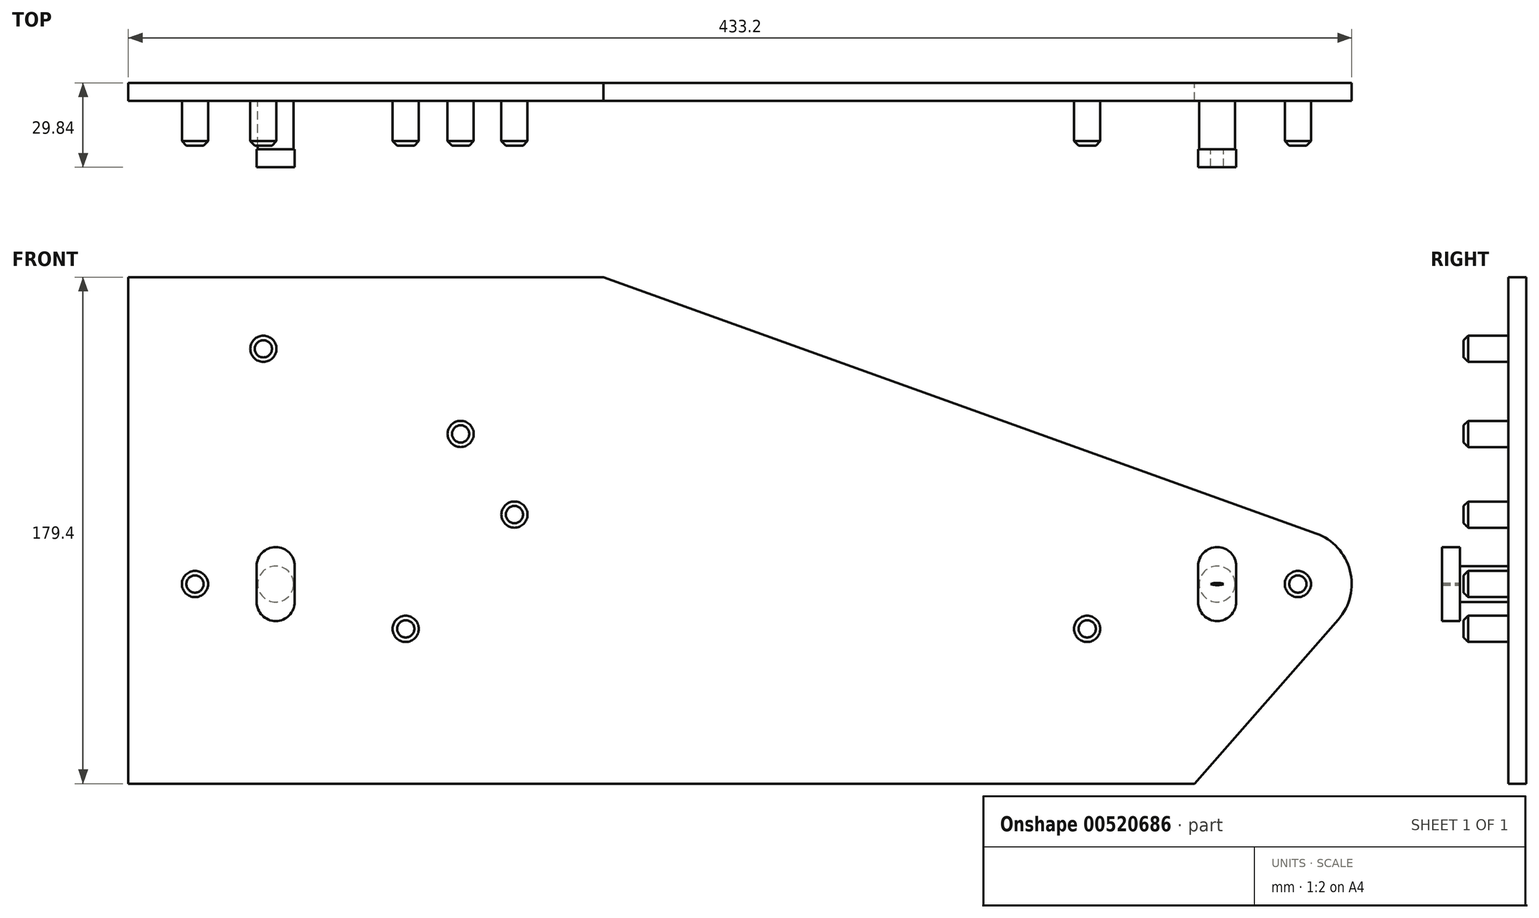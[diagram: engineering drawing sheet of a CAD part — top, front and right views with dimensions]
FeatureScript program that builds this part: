
annotation { "Feature Type Name" : "Feature", "Feature Type Description" : "" }
export const myFeature = defineFeature(function(context is Context, id is Id, definition is map)
    precondition{}
    {
        {
            var Q0;
            Q0=qCreatedBy(makeId("Front.planeOp"),FACE);
            var sketch = newSketch(context, id + "F0", { "sketchPlane" : qUnion([Q0])});
            skLineSegment(sketch, "E0", {"start": v(0, 0) * mm, "end": v(0, 179.4) * mm});
            skLineSegment(sketch, "E1", {"start": v(0, 0) * mm, "end": v(377.52, 0) * mm});
            skLineSegment(sketch, "E2", {"start": v(0, 179.4) * mm, "end": v(168.28, 179.4) * mm});
            skLineSegment(sketch, "E3", {"start": v(168.27, 179.4) * mm, "end": v(420.6, 88.65) * mm});
            skLineSegment(sketch, "E4", {"start": v(377.52, 0) * mm, "end": v(428.48, 58.18) * mm});
            skPoint(sketch, "E5.visualSharp", {"position": v(446.89, 79.2) * mm});
            skArc(sketch, "E5.filletArc", {"start": v(428.48, 58.18) * mm, "mid": v(432.59, 75.5) * mm, "end": v(420.6, 88.65) * mm});
            skSolve(sketch);
        }
        {
            var Q0;
            Q0 = qSketchRegion(id + "F0", true);
            extrude(context, id + "F1", {"entities" : qUnion([Q0]), "endBound" : BoundingType.SYMMETRIC, "depth" : 6.35 * mm, "offsetDistance" : 25.4 * mm});
        }
        {
            var Q0;
            Q0=makeQuery(id+"F1.opExtrude","CAP_FACE",FACE,{"disambiguationData":[OSD([sQuery(id+"F0.wireOp",EDGE,"E0"),sQuery(id+"F0.wireOp",EDGE,"E1"),sQuery(id+"F0.wireOp",EDGE,"E2"),sQuery(id+"F0.wireOp",EDGE,"E3"),sQuery(id+"F0.wireOp",EDGE,"E4"),sQuery(id+"F0.wireOp",EDGE,"E5.filletArc")])],"isStart":false});
            var sketch = newSketch(context, id + "F2", { "sketchPlane" : qUnion([Q0])});
            skCircle(sketch, "E6", {"center": v(23.62, 70.71) * mm, "radius": 4.64 * mm});
            skCircle(sketch, "E7", {"center": v(98.22, 54.84) * mm, "radius": 4.64 * mm});
            skCircle(sketch, "E8", {"center": v(339.52, 54.84) * mm, "radius": 4.64 * mm});
            skCircle(sketch, "E9", {"center": v(136.73, 95.33) * mm, "radius": 4.64 * mm});
            skCircle(sketch, "E10", {"center": v(47.83, 154.05) * mm, "radius": 4.64 * mm});
            skCircle(sketch, "E11", {"center": v(117.68, 123.9) * mm, "radius": 4.64 * mm});
            skCircle(sketch, "E12", {"center": v(414.15, 70.71) * mm, "radius": 4.64 * mm});
            skSolve(sketch);
        }
        {
            var Q0;
            Q0 = qSketchRegion(id + "F2", true);
            extrude(context, id + "F3", {"entities" : qUnion([Q0]), "operationType" : NewBodyOperationType.ADD, "depth" : 15.88 * mm, "offsetDistance" : 25.4 * mm});
        }
        {
            var Q0;
            Q0=makeQuery(id+"F3.opExtrude","CAP_EDGE",EDGE,{"disambiguationData":[OSD([sQuery(id+"F2.wireOp",EDGE,"E6")])],"isStart":false});
            var Q1;
            Q1=makeQuery(id+"F3.opExtrude","CAP_EDGE",EDGE,{"disambiguationData":[OSD([sQuery(id+"F2.wireOp",EDGE,"E10")])],"isStart":false});
            var Q2;
            Q2=makeQuery(id+"F3.opExtrude","CAP_EDGE",EDGE,{"disambiguationData":[OSD([sQuery(id+"F2.wireOp",EDGE,"E7")])],"isStart":false});
            var Q3;
            Q3=makeQuery(id+"F3.opExtrude","CAP_EDGE",EDGE,{"disambiguationData":[OSD([sQuery(id+"F2.wireOp",EDGE,"E11")])],"isStart":false});
            var Q4;
            Q4=makeQuery(id+"F3.opExtrude","CAP_EDGE",EDGE,{"disambiguationData":[OSD([sQuery(id+"F2.wireOp",EDGE,"E9")])],"isStart":false});
            var Q5;
            Q5=makeQuery(id+"F3.opExtrude","CAP_EDGE",EDGE,{"disambiguationData":[OSD([sQuery(id+"F2.wireOp",EDGE,"E8")])],"isStart":false});
            var Q6;
            Q6=makeQuery(id+"F3.opExtrude","CAP_EDGE",EDGE,{"disambiguationData":[OSD([sQuery(id+"F2.wireOp",EDGE,"E12")])],"isStart":false});
            chamfer(context, id + "F4", {"entities" : qUnion([Q0, Q1, Q2, Q3, Q4, Q5, Q6]), "width" : 1.59 * mm, "tangentPropagation" : true});
        }
        {
            var Q0;
            Q0=makeQuery(id+"F1.opExtrude","CAP_FACE",FACE,{"disambiguationData":[OSD([sQuery(id+"F0.wireOp",EDGE,"E0"),sQuery(id+"F0.wireOp",EDGE,"E1"),sQuery(id+"F0.wireOp",EDGE,"E2"),sQuery(id+"F0.wireOp",EDGE,"E3"),sQuery(id+"F0.wireOp",EDGE,"E4"),sQuery(id+"F0.wireOp",EDGE,"E5.filletArc")])],"isStart":false});
            var sketch = newSketch(context, id + "F5", { "sketchPlane" : qUnion([Q0])});
            skSolve(sketch);
        }
        {
            var Q0;
            Q0=makeQuery(id+"F5.imprint","IMPRINT",FACE,{"disambiguationData":[TD([[makeQuery(id+"F5.imprint","IMPRINT",EDGE,{"derivedFrom":makeQuery(id+"F1.opExtrude","CAP_EDGE",EDGE,{"disambiguationData":[OSD([sQuery(id+"F0.wireOp",EDGE,"E0")])],"isStart":false})}),-1.0]])]});
            var sketch = newSketch(context, id + "F6", { "sketchPlane" : qUnion([Q0])});
            skCircle(sketch, "E13", {"center": v(385.57, 70.71) * mm, "radius": 6.35 * mm});
            skCircle(sketch, "E14", {"center": v(52.2, 70.71) * mm, "radius": 6.35 * mm});
            skSolve(sketch);
        }
        {
            var Q0;
            Q0 = qSketchRegion(id + "F6", true);
            extrude(context, id + "F7", {"entities" : qUnion([Q0]), "operationType" : NewBodyOperationType.ADD, "depth" : 17.14 * mm, "offsetDistance" : 25.4 * mm});
        }
        {
            var Q0;
            Q0=makeQuery(id+"F7.opExtrude","CAP_FACE",FACE,{"disambiguationData":[OSD([sQuery(id+"F6.wireOp",EDGE,"E14")])],"isStart":false});
            var sketch = newSketch(context, id + "F8", { "sketchPlane" : qUnion([Q0])});
            skLineSegment(sketch, "E15", {"start": v(45.45, 77.06) * mm, "end": v(45.45, 64.36) * mm});
            skLineSegment(sketch, "E16", {"start": v(58.94, 77.06) * mm, "end": v(58.94, 64.36) * mm});
            skArc(sketch, "E17.trimOffspring", {"start": v(58.94, 77.06) * mm, "mid": v(52.2, 83.8) * mm, "end": v(45.45, 77.06) * mm});
            skArc(sketch, "E18.trimOffspring", {"start": v(45.45, 64.36) * mm, "mid": v(52.2, 57.62) * mm, "end": v(58.94, 64.36) * mm});
            skLineSegment(sketch, "E19", {"start": v(52.2, 77.06) * mm, "end": v(52.2, 64.36) * mm, "construction": true});
            skLineSegment(sketch, "E20", {"start": v(52.2, 70.71) * mm, "end": v(45.85, 70.71) * mm, "construction": true});
            skSolve(sketch);
        }
        {
            var Q0;
            Q0 = qSketchRegion(id + "F8", true);
            extrude(context, id + "F9", {"entities" : qUnion([Q0]), "operationType" : NewBodyOperationType.ADD, "depth" : 6.35 * mm, "offsetDistance" : 25.4 * mm});
        }
        {
            var Q0;
            Q0=makeQuery(id+"F7.opExtrude","CAP_FACE",FACE,{"disambiguationData":[OSD([sQuery(id+"F6.wireOp",EDGE,"E13")])],"isStart":false});
            var sketch = newSketch(context, id + "F10", { "sketchPlane" : qUnion([Q0])});
            skLineSegment(sketch, "E21", {"start": v(385.57, 70.71) * mm, "end": v(385.57, 77.06) * mm, "construction": true});
            skLineSegment(sketch, "E22", {"start": v(385.57, 70.71) * mm, "end": v(379.22, 70.71) * mm, "construction": true});
            skCircle(sketch, "E23", {"center": v(385.57, 77.06) * mm, "radius": 6.74 * mm});
            skCircle(sketch, "E24", {"center": v(385.57, 64.36) * mm, "radius": 6.74 * mm});
            skLineSegment(sketch, "E25", {"start": v(385.57, 77.06) * mm, "end": v(385.57, 64.36) * mm, "construction": true});
            skLineSegment(sketch, "E26", {"start": v(378.83, 77.06) * mm, "end": v(378.83, 64.36) * mm});
            skLineSegment(sketch, "E27", {"start": v(392.32, 77.06) * mm, "end": v(392.32, 64.36) * mm});
            skSolve(sketch);
        }
        {
            var Q0;
            Q0 = qSketchRegion(id + "F10", true);
            var Q1;
            {var subQ0=sQuery(id+"F10.wireOp",EDGE,"E24");var subQ1=sQuery(id+"F10.wireOp",EDGE,"E23");var subQ2=makeQuery(id+"F10.imprint","INTERSECT",VERTEX,{"disambiguationData":[OD(0.0)],"derivedFrom":[subQ1,subQ0]});Q1=makeQuery(id+"F10.imprint","IMPRINT",FACE,{"disambiguationData":[TD([[makeQuery(id+"F10.imprint","IMPRINT",EDGE,{"disambiguationData":[TD([[subQ2,-1.0]])],"derivedFrom":subQ1}),1.0]])]});}
            extrude(context, id + "F11", {"entities" : qUnion([Q0, Q1]), "operationType" : NewBodyOperationType.ADD, "depth" : 6.35 * mm, "offsetDistance" : 25.4 * mm});
        }
    });
